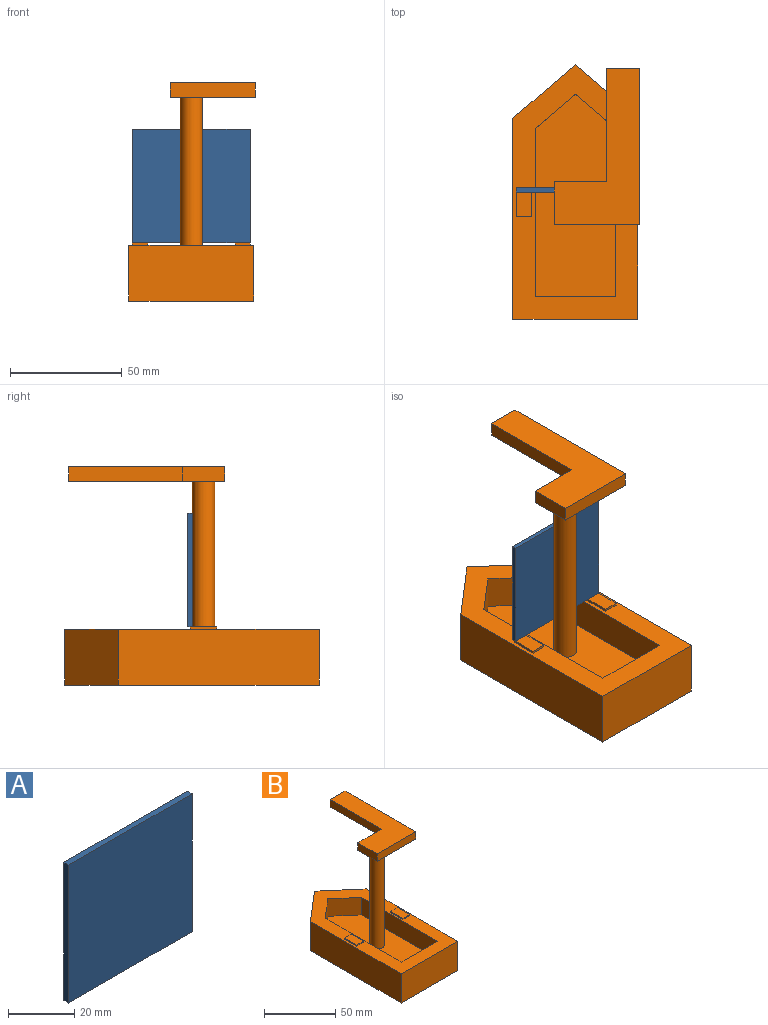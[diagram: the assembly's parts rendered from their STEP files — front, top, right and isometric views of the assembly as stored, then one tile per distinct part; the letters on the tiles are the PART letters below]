
ASSEMBLY  parts=2 mates=1
PART A: 6 faces, bbox 52.7x2x50.8 mm
  f0: plane 52.65x2mm, normal (0,0,1), area 105.3mm2, adj f1,f3,f4,f5
  f1: plane 52.65x50.8mm, normal (0,-1,0), area 2674.8mm2, adj f0,f2,f4,f5
  f2: plane 52.65x2mm, normal (0,0,-1), area 105.3mm2, adj f1,f3,f4,f5
  f3: plane 52.65x50.8mm, normal (0,1,0), area 2674.8mm2, adj f0,f2,f4,f5
  f4: plane 50.8x2mm, normal (1,0,0), area 101.6mm2, adj f0,f1,f2,f3
  f5: plane 50.8x2mm, normal (-1,0,0), area 101.6mm2, adj f0,f1,f2,f3
PART B: 32 faces, bbox 56.5x113.9x97.6 mm
  f0: plane 113.93x55.88mm, normal (0,0,1), area 2554.7mm2, adj f1,f2,f3,f4,f5,f7,f8,f9
  f1: plane 27.94x25mm, normal (-0.65,0.76,0), area 921mm2, adj f0,f2,f5,f6
  f2: plane 89.92x25mm, normal (-1,0,0), area 2248mm2, adj f0,f1,f3,f6
  f3: plane 55.88x25mm, normal (0,-1,0), area 1397mm2, adj f0,f2,f4,f6
  f4: plane 89.92x25mm, normal (1,0,0), area 2248mm2, adj f0,f3,f5,f6
  f5: plane 27.94x25mm, normal (0.65,0.76,0), area 921mm2, adj f0,f1,f4,f6
  f6: plane 113.93x55.88mm, normal (0,0,-1), area 5695.7mm2, adj f1,f2,f3,f4,f5
  f7: plane 17.94x15.42mm, normal (0.65,-0.76,0), area 354.8mm2, adj f0,f8,f11,f12
  f8: plane 75.33x15mm, normal (1,0,0), area 1129.9mm2, adj f0,f7,f9,f12
  f9: plane 35.88x15mm, normal (0,1,0), area 538.2mm2, adj f0,f8,f10,f12
  f10: plane 75.33x15mm, normal (-1,0,0), area 1129.9mm2, adj f0,f9,f11,f12
  f11: plane 17.94x15.42mm, normal (-0.65,-0.76,0), area 354.8mm2, adj f0,f7,f10,f12
  f12: plane 90.75x35.88mm, normal (0,0,1), area 2900.9mm2, adj f7,f8,f9,f10,f11,f13
  f13: cylinder r=5mm len=81.28mm, axis (0,0,-1), area 2553.5mm2, adj f12,f28
  f14: plane 6.73x1mm, normal (0,-1,0), area 6.7mm2, adj f0,f15,f17,f18
  f15: plane 12x1mm, normal (1,0,0), area 12mm2, adj f0,f14,f16,f18
  f16: plane 6.73x1mm, normal (0,1,0), area 6.7mm2, adj f0,f15,f17,f18
  f17: plane 12x1mm, normal (-1,0,0), area 12mm2, adj f0,f14,f16,f18
  f18: plane 12x6.73mm, normal (0,0,1), area 80.8mm2, adj f14,f15,f16,f17
  f19: plane 12x1mm, normal (-1,0,0), area 12mm2, adj f0,f20,f22,f23
  f20: plane 6.73x1mm, normal (0,-1,0), area 6.7mm2, adj f0,f19,f21,f23
  f21: plane 12x1mm, normal (1,0,0), area 12mm2, adj f0,f20,f22,f23
  f22: plane 6.73x1mm, normal (0,1,0), area 6.7mm2, adj f0,f19,f21,f23
  f23: plane 12x6.73mm, normal (0,0,1), area 80.8mm2, adj f19,f20,f21,f22
  f24: plane 23.32x6.35mm, normal (0,1,0), area 148.1mm2, adj f25,f27,f28,f30
  f25: plane 19.05x6.35mm, normal (-1,0,0), area 121mm2, adj f24,f26,f27,f28
  f26: plane 38.1x6.35mm, normal (0,-1,0), area 241.9mm2, adj f25,f27,f28,f29
  f27: plane 69.85x38.1mm, normal (0,0,1), area 1476.7mm2, adj f24,f25,f26,f29,f30,f31
  f28: plane 69.85x38.1mm, normal (0,0,-1), area 1398.2mm2, adj f13,f24,f25,f26,f29,f30,f31
  f29: plane 69.85x6.35mm, normal (1,0,0), area 443.5mm2, adj f26,f27,f28,f31
  f30: plane 50.8x6.35mm, normal (-1,0,0), area 322.6mm2, adj f24,f27,f28,f31
  f31: plane 14.78x6.35mm, normal (0,1,0), area 93.9mm2, adj f27,f28,f29,f30
PLACE A t=(0.01,20.4,22.09)mm
PLACE B t=(0,0.62,12.5)mm
MATE fastened A.f2 <-> B.f18  axis (0,0,-1) through (-26.32,6.62,26)mm
